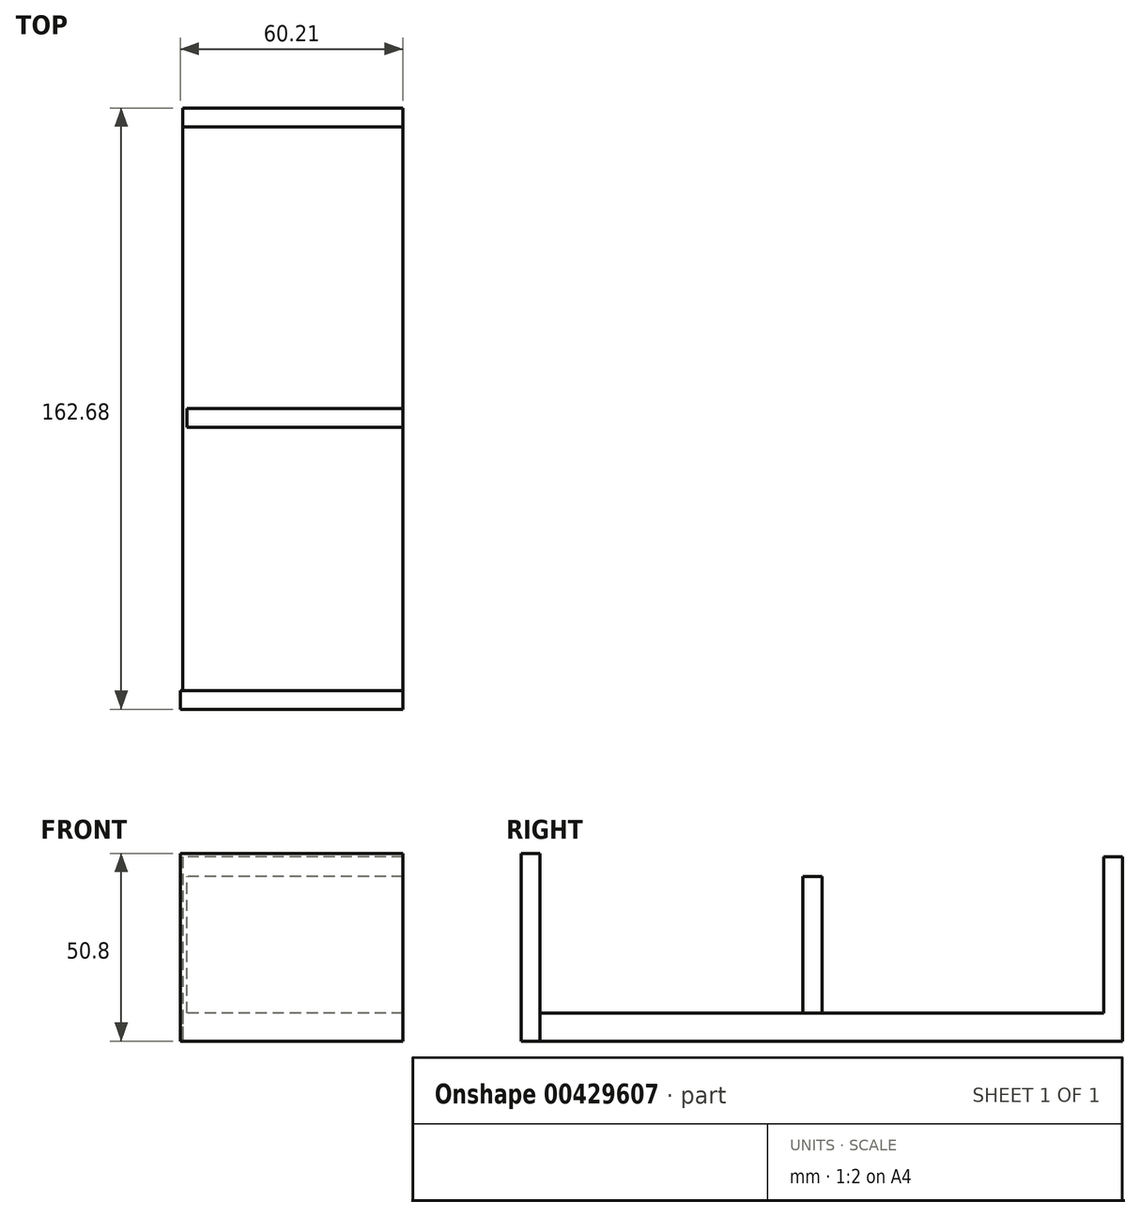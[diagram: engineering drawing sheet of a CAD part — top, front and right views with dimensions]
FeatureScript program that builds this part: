
annotation { "Feature Type Name" : "Feature", "Feature Type Description" : "" }
export const myFeature = defineFeature(function(context is Context, id is Id, definition is map)
    precondition{}
    {
        {
            var Q0;
            Q0=qCreatedBy(makeId("Top.planeOp"),FACE);
            var sketch = newSketch(context, id + "F0", { "sketchPlane" : qUnion([Q0])});
            skLineSegment(sketch, "E0.bottom", {"start": v(29.8, 76.26) * mm, "end": v(-29.8, 76.26) * mm});
            skLineSegment(sketch, "E0.top", {"start": v(29.8, -76.26) * mm, "end": v(-29.8, -76.26) * mm});
            skLineSegment(sketch, "E0.left", {"start": v(29.8, 76.26) * mm, "end": v(29.8, -76.26) * mm});
            skLineSegment(sketch, "E0.right", {"start": v(-29.8, 76.26) * mm, "end": v(-29.8, -76.26) * mm});
            skPoint(sketch, "E0.middle", {"position": v(0, 0) * mm});
            skSolve(sketch);
        }
        {
            var Q0;
            Q0 = qSketchRegion(id + "F0", true);
            extrude(context, id + "F1", {"entities" : qUnion([Q0]), "depth" : 7.62 * mm});
        }
        {
            var Q0;
            Q0=makeQuery(id+"F1.opExtrude","SWEPT_FACE",FACE,{"disambiguationData":[OSD([sQuery(id+"F0.wireOp",EDGE,"E0.top")])]});
            cPlane(context, id + "F2", {"entities" : qUnion([Q0]), "cplaneType" : CPlaneType.OFFSET, "offset" : 0 * mm, "width" : 152.4 * mm, "height" : 152.4 * mm});
        }
        {
            var Q0;
            Q0=qCreatedBy(id+"F2.planeOp",FACE);
            var sketch = newSketch(context, id + "F3", { "sketchPlane" : qUnion([Q0])});
            skLineSegment(sketch, "E1.bottom", {"start": v(29.77, 0) * mm, "end": v(-30.41, 0) * mm});
            skLineSegment(sketch, "E1.top", {"start": v(29.77, 50.8) * mm, "end": v(-30.41, 50.8) * mm});
            skLineSegment(sketch, "E1.left", {"start": v(29.77, 0) * mm, "end": v(29.77, 50.8) * mm});
            skLineSegment(sketch, "E1.right", {"start": v(-30.41, 0) * mm, "end": v(-30.41, 50.8) * mm});
            skSolve(sketch);
        }
        {
            var Q0;
            Q0=makeQuery(id+"F3.imprint","IMPRINT",FACE,{"disambiguationData":[TD([[makeQuery(id+"F3.imprint","IMPRINT",EDGE,{"derivedFrom":sQuery(id+"F3.wireOp",EDGE,"E1.bottom")}),-1.0]])]});
            extrude(context, id + "F4", {"entities" : qUnion([Q0]), "operationType" : NewBodyOperationType.ADD, "depth" : 5.08 * mm, "offsetDistance" : 25.4 * mm});
        }
        {
            var Q0;
            Q0=qCreatedBy(makeId("Front.planeOp"),FACE);
            var sketch = newSketch(context, id + "F5", { "sketchPlane" : qUnion([Q0])});
            skLineSegment(sketch, "E2.bottom", {"start": v(29.8, 7.62) * mm, "end": v(-28.61, 7.62) * mm});
            skLineSegment(sketch, "E2.top", {"start": v(29.8, 44.55) * mm, "end": v(-28.61, 44.55) * mm});
            skLineSegment(sketch, "E2.left", {"start": v(29.8, 7.62) * mm, "end": v(29.8, 44.55) * mm});
            skLineSegment(sketch, "E2.right", {"start": v(-28.61, 7.62) * mm, "end": v(-28.61, 44.55) * mm});
            skSolve(sketch);
        }
        {
            var Q0;
            Q0 = qSketchRegion(id + "F5", true);
            extrude(context, id + "F6", {"entities" : qUnion([Q0]), "depth" : 5.08 * mm, "offsetDistance" : 25.4 * mm});
        }
        {
            var Q0;
            Q0=makeQuery(id+"F1.opExtrude","SWEPT_FACE",FACE,{"disambiguationData":[OSD([sQuery(id+"F0.wireOp",EDGE,"E0.bottom")])]});
            var sketch = newSketch(context, id + "F7", { "sketchPlane" : qUnion([Q0])});
            skPoint(sketch, "E3.oppositeSnap0", {"position": v(29.8, 3.81) * mm});
            skLineSegment(sketch, "E3.bottom", {"start": v(-29.8, 0) * mm, "end": v(29.8, 0) * mm});
            skLineSegment(sketch, "E3.top", {"start": v(-29.8, 49.87) * mm, "end": v(29.8, 49.87) * mm});
            skLineSegment(sketch, "E3.left", {"start": v(-29.8, 0) * mm, "end": v(-29.8, 49.87) * mm});
            skLineSegment(sketch, "E3.right", {"start": v(29.8, 0) * mm, "end": v(29.8, 49.87) * mm});
            skSolve(sketch);
        }
        {
            var Q0;
            Q0 = qSketchRegion(id + "F7", true);
            extrude(context, id + "F8", {"entities" : qUnion([Q0]), "operationType" : NewBodyOperationType.ADD, "depth" : 5.08 * mm, "offsetDistance" : 25.4 * mm});
        }
    });
